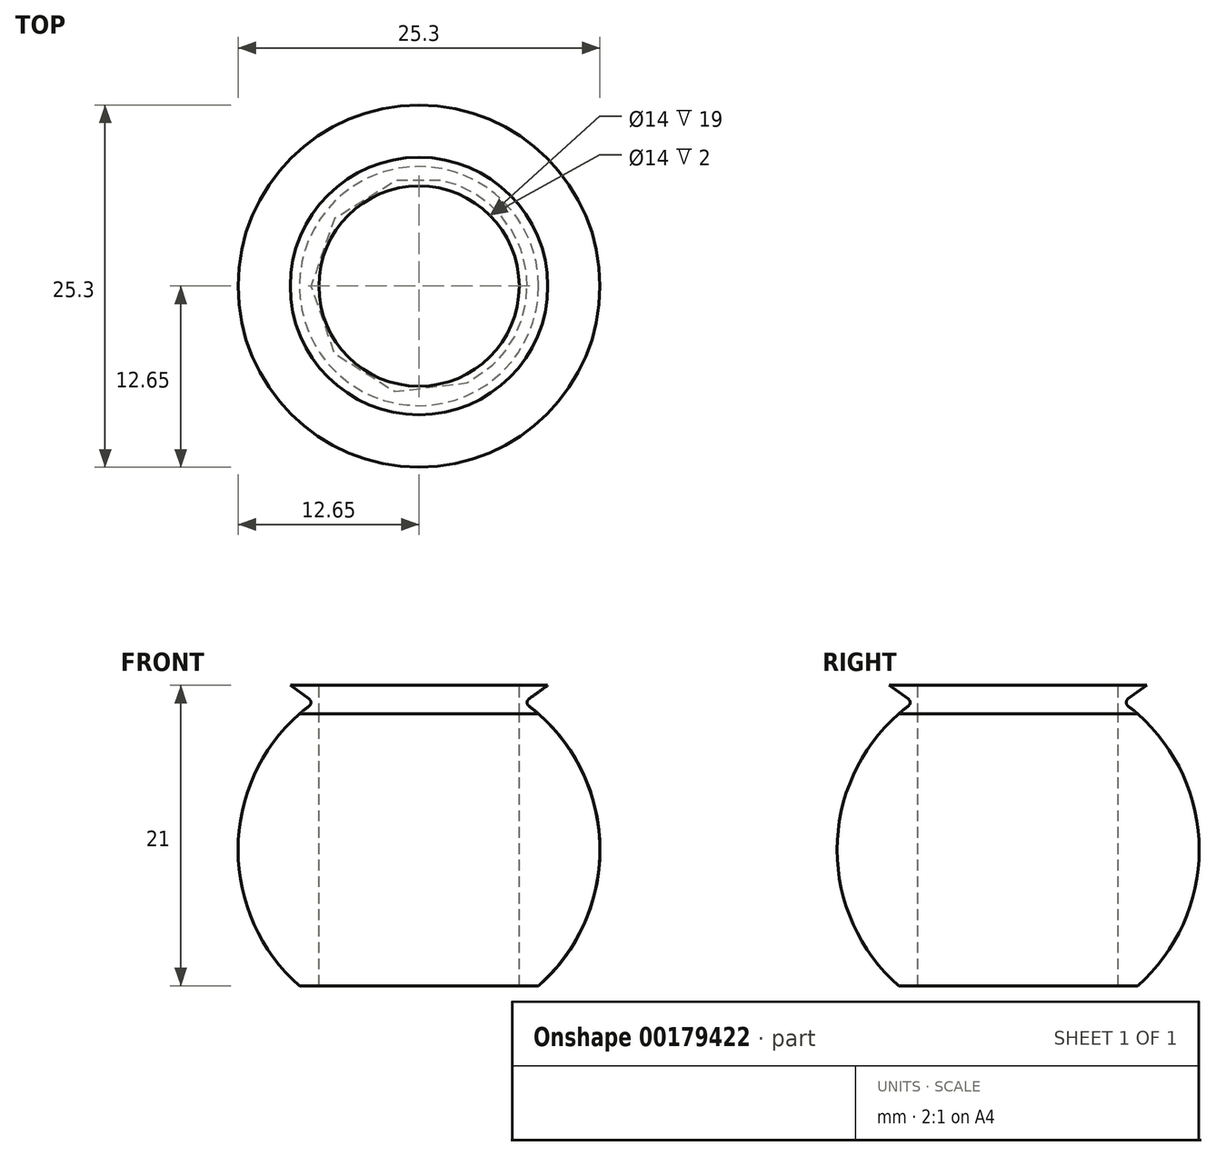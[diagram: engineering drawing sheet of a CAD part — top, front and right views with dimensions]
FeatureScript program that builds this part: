
annotation { "Feature Type Name" : "Feature", "Feature Type Description" : "" }
export const myFeature = defineFeature(function(context is Context, id is Id, definition is map)
    precondition{}
    {
        {
            var Q0;
            Q0=qCreatedBy(makeId("Front.planeOp"),FACE);
            var sketch = newSketch(context, id + "F0", { "sketchPlane" : qUnion([Q0])});
            skArc(sketch, "E0", {"start": v(-7, 10.54) * mm, "mid": v(0, -12.65) * mm, "end": v(7, 10.54) * mm});
            skLineSegment(sketch, "E1.bottom", {"start": v(25.95, -9.5) * mm, "end": v(-25.95, -9.5) * mm});
            skLineSegment(sketch, "E1.top", {"start": v(25.95, 9.5) * mm, "end": v(7, 9.5) * mm});
            skLineSegment(sketch, "E1.left", {"start": v(25.95, -9.5) * mm, "end": v(25.95, 9.5) * mm});
            skLineSegment(sketch, "E1.right", {"start": v(-25.95, -9.5) * mm, "end": v(-25.95, 9.5) * mm});
            skLineSegment(sketch, "E2.bottom", {"start": v(7, -21) * mm, "end": v(-7, -21) * mm});
            skLineSegment(sketch, "E2.top", {"start": v(7, 21) * mm, "end": v(-7, 21) * mm});
            skLineSegment(sketch, "E2.left", {"start": v(7, -21) * mm, "end": v(7, 21) * mm});
            skLineSegment(sketch, "E2.right", {"start": v(-7, -21) * mm, "end": v(-7, 21) * mm});
            skLineSegment(sketch, "E3.trimOffspring", {"start": v(-7, 9.5) * mm, "end": v(-25.95, 9.5) * mm});
            skLineSegment(sketch, "E4", {"start": v(-19.36, 11.5) * mm, "end": v(32.33, 11.5) * mm});
            skPoint(sketch, "E5", {"position": v(7.34, 10.3) * mm});
            skLineSegment(sketch, "E6", {"start": v(7.34, 10.3) * mm, "end": v(9, 11.5) * mm});
            skLineSegment(sketch, "E7", {"start": v(0, 25.16) * mm, "end": v(0, -6.2) * mm});
            skSolve(sketch);
        }
        {
            var Q0;
            {var subQ3=sQuery(id+"F0.wireOp",EDGE,"E6");Q0=makeQuery(id+"F0.imprint","IMPRINT",FACE,{"disambiguationData":[TD([[makeQuery(id+"F0.imprint","IMPRINT",EDGE,{"derivedFrom":subQ3}),1.0]])]});}
            var Q1;
            {var subQ0=sQuery(id+"F0.wireOp",EDGE,"E0");var subQ1=makeQuery(id+"F0.imprint","INTERSECT",VERTEX,{"derivedFrom":[subQ0,sQuery(id+"F0.wireOp",EDGE,"E6")]});Q1=makeQuery(id+"F0.imprint","IMPRINT",FACE,{"disambiguationData":[TD([[makeQuery(id+"F0.imprint","IMPRINT",EDGE,{"disambiguationData":[TD([[subQ1,1.0]])],"derivedFrom":subQ0}),1.0]])]});}
            var Q2;
            Q2=sQuery(id+"F0.wireOp",EDGE,"E7");
            revolve(context, id + "F1", {"entities" : qUnion([Q0, Q1]), "axis" : qUnion([Q2]), "revolveType" : RevolveType.FULL});
        }
        {
            var Q0;
            Q0=makeQuery(id+"F1.opRevolve","SWEPT_EDGE",EDGE,{"disambiguationData":[OSD([sQuery(id+"F0.wireOp",EDGE,"E0"),sQuery(id+"F0.wireOp",EDGE,"E6")])]});
            fillet(context, id + "F2", {"entities" : qUnion([Q0]), "radius" : 0.3 * mm, "tangentPropagation" : true, "allowEdgeOverflow" : false});
        }
        {
            var Q0;
            {var subQ0=sQuery(id+"F0.wireOp",EDGE,"E1.bottom");var subQ1=sQuery(id+"F0.wireOp",EDGE,"E0");var subQ2=makeQuery(id+"F0.imprint","INTERSECT",VERTEX,{"disambiguationData":[OD(1.0)],"derivedFrom":[subQ1,subQ0]});Q0=makeQuery(id+"F0.imprint","IMPRINT",FACE,{"disambiguationData":[TD([[makeQuery(id+"F0.imprint","IMPRINT",EDGE,{"disambiguationData":[TD([[subQ2,-1.0]])],"derivedFrom":subQ1}),1.0]])]});}
            var Q1;
            Q1=sQuery(id+"F0.wireOp",EDGE,"E7");
            revolve(context, id + "F3", {"entities" : qUnion([Q0]), "axis" : qUnion([Q1]), "revolveType" : RevolveType.FULL});
        }
    });
